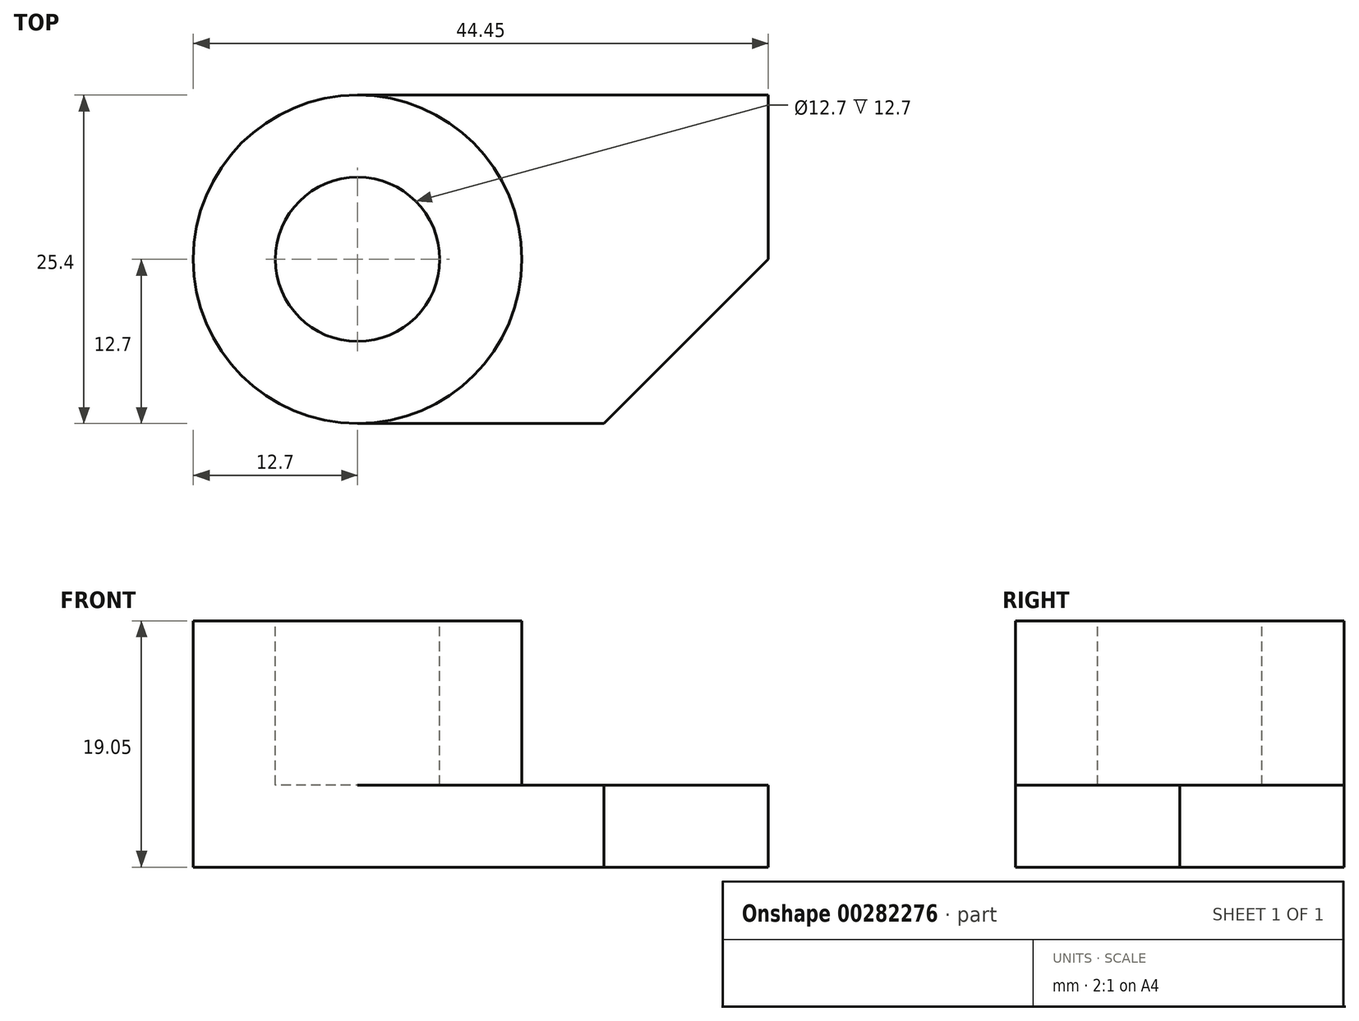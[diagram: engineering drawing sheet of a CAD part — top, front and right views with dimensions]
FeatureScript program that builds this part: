
annotation { "Feature Type Name" : "Feature", "Feature Type Description" : "" }
export const myFeature = defineFeature(function(context is Context, id is Id, definition is map)
    precondition{}
    {
        {
            var Q0;
            Q0=qCreatedBy(makeId("Top.planeOp"),FACE);
            var sketch = newSketch(context, id + "F0", { "sketchPlane" : qUnion([Q0])});
            skCircle(sketch, "E0", {"center": v(0, 0) * mm, "radius": 12.7 * mm});
            skSolve(sketch);
        }
        {
            var Q0;
            Q0 = qSketchRegion(id + "F0", true);
            extrude(context, id + "F1", {"entities" : qUnion([Q0]), "depth" : 19.05 * mm});
        }
        {
            var Q0;
            Q0=makeQuery(id+"F1.opExtrude","CAP_FACE",FACE,{"disambiguationData":[OSD([sQuery(id+"F0.wireOp",EDGE,"E0")])],"isStart":false});
            var sketch = newSketch(context, id + "F2", { "sketchPlane" : qUnion([Q0])});
            skCircle(sketch, "E1", {"center": v(0, 0) * mm, "radius": 6.35 * mm});
            skSolve(sketch);
        }
        {
            var Q0;
            Q0 = qSketchRegion(id + "F2", true);
            extrude(context, id + "F3", {"entities" : qUnion([Q0]), "operationType" : NewBodyOperationType.REMOVE, "oppositeDirection" : true, "depth" : 19.05 * mm});
        }
        {
            var Q0;
            Q0=qCreatedBy(makeId("Top.planeOp"),FACE);
            var sketch = newSketch(context, id + "F4", { "sketchPlane" : qUnion([Q0])});
            skLineSegment(sketch, "E2", {"start": v(0, 12.7) * mm, "end": v(31.75, 12.7) * mm});
            skLineSegment(sketch, "E3", {"start": v(31.75, 12.7) * mm, "end": v(31.75, 0) * mm});
            skLineSegment(sketch, "E4", {"start": v(31.75, 0) * mm, "end": v(19.05, -12.7) * mm});
            skLineSegment(sketch, "E5", {"start": v(19.05, -12.7) * mm, "end": v(0, -12.7) * mm});
            skArc(sketch, "E6", {"start": v(0, 12.7) * mm, "mid": v(-12.7, 0) * mm, "end": v(0, -12.7) * mm});
            skSolve(sketch);
        }
        {
            var Q0;
            Q0 = qSketchRegion(id + "F4", true);
            extrude(context, id + "F5", {"entities" : qUnion([Q0]), "operationType" : NewBodyOperationType.ADD, "depth" : 6.35 * mm});
        }
    });
